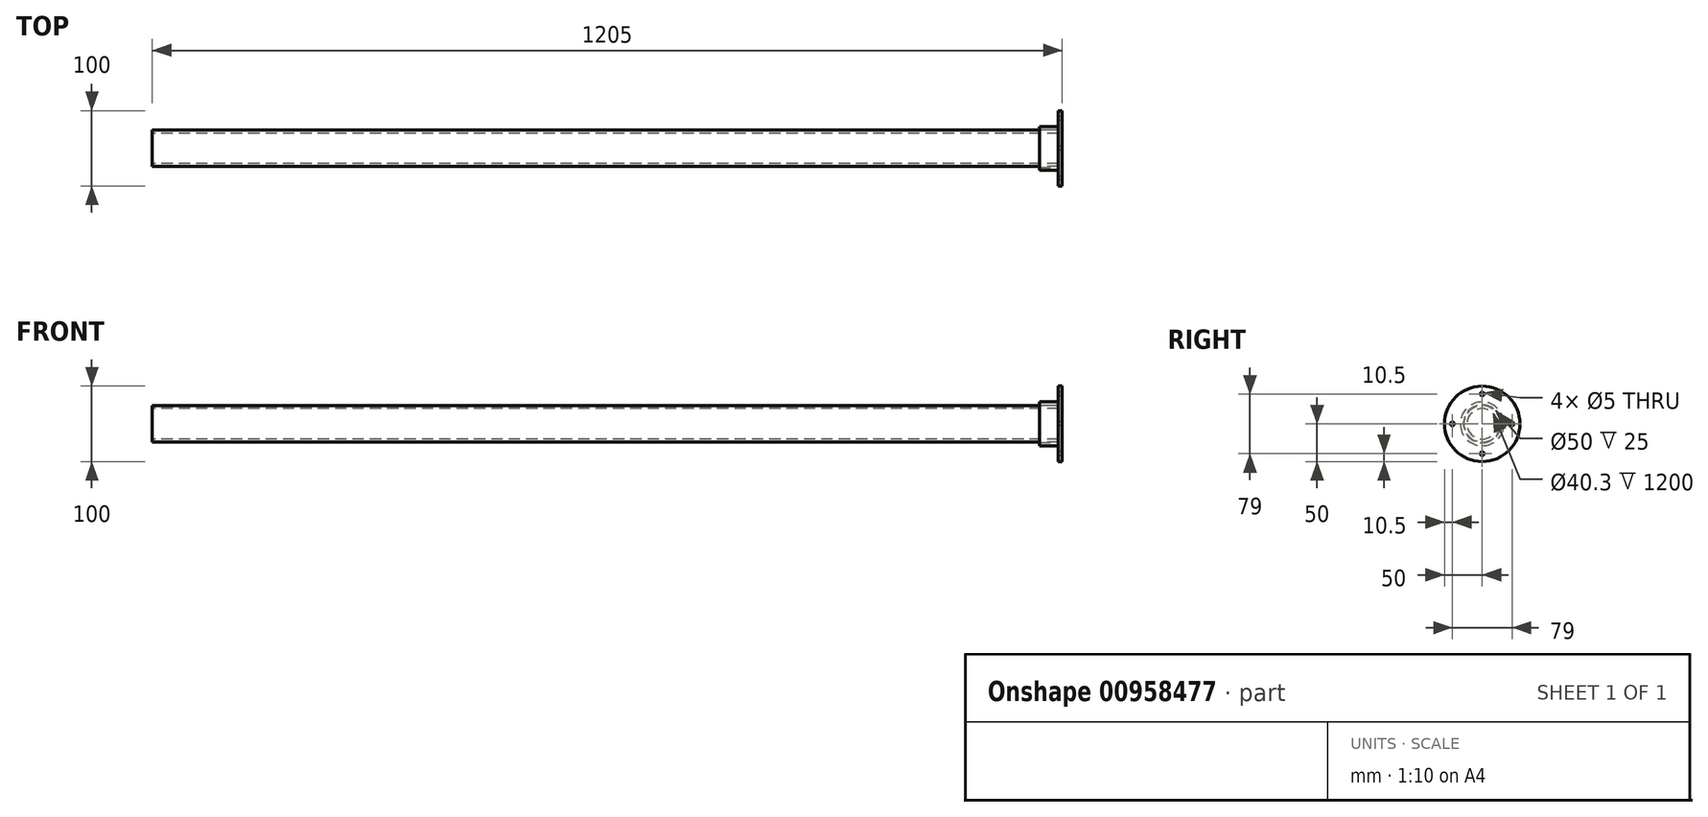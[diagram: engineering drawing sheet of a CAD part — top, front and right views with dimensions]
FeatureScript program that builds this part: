
annotation { "Feature Type Name" : "Feature", "Feature Type Description" : "" }
export const myFeature = defineFeature(function(context is Context, id is Id, definition is map)
    precondition{}
    {
        {
            var Q0;
            Q0=qCreatedBy(makeId("Right.planeOp"),FACE);
            var sketch = newSketch(context, id + "F0", { "sketchPlane" : qUnion([Q0])});
            skCircle(sketch, "E0", {"center": v(0, 0) * mm, "radius": 24.15 * mm});
            skCircle(sketch, "E1", {"center": v(0, 0) * mm, "radius": 20.15 * mm});
            skSolve(sketch);
        }
        {
            var Q0;
            Q0 = qSketchRegion(id + "F0", true);
            extrude(context, id + "F1", {"entities" : qUnion([Q0]), "depth" : 1200 * mm, "offsetDistance" : 25 * mm});
        }
        {
            var Q0;
            Q0=makeQuery(id+"F1.opExtrude","CAP_FACE",FACE,{"disambiguationData":[OSD([sQuery(id+"F0.wireOp",EDGE,"E0"),sQuery(id+"F0.wireOp",EDGE,"E1")])],"isStart":false});
            var sketch = newSketch(context, id + "F2", { "sketchPlane" : qUnion([Q0])});
            skCircle(sketch, "E2", {"center": v(0, 0) * mm, "radius": 50 * mm});
            skSolve(sketch);
        }
        {
            var Q0;
            Q0 = qSketchRegion(id + "F2", true);
            extrude(context, id + "F3", {"entities" : qUnion([Q0]), "depth" : 5 * mm, "offsetDistance" : 25 * mm});
        }
        {
            var Q0;
            Q0=makeQuery(id+"F3.opExtrude","CAP_FACE",FACE,{"disambiguationData":[OSD([sQuery(id+"F2.wireOp",EDGE,"E2")])],"isStart":true});
            var sketch = newSketch(context, id + "F4", { "sketchPlane" : qUnion([Q0])});
            skCircle(sketch, "E3", {"center": v(0, 0) * mm, "radius": 25 * mm});
            skCircle(sketch, "E4", {"center": v(0, 0) * mm, "radius": 29 * mm});
            skSolve(sketch);
        }
        {
            var Q0;
            Q0 = qSketchRegion(id + "F4", true);
            extrude(context, id + "F5", {"entities" : qUnion([Q0]), "operationType" : NewBodyOperationType.ADD, "depth" : 25 * mm, "offsetDistance" : 25 * mm});
        }
        {
            var Q0;
            {var subQ0=sQuery(id+"F2.wireOp",EDGE,"E2");Q0=makeQuery(id+"F5.boolean.opBoolean","SPLIT",FACE,{"disambiguationData":[TD([makeQuery(id+"F3.opExtrude","SWEPT_FACE",FACE,{"disambiguationData":[OSD([subQ0])]})])],"derivedFrom":makeQuery(id+"F3.opExtrude","CAP_FACE",FACE,{"disambiguationData":[OSD([subQ0])],"isStart":true})});}
            var sketch = newSketch(context, id + "F6", { "sketchPlane" : qUnion([Q0])});
            skCircle(sketch, "E5", {"center": v(0, 0) * mm, "radius": 39.5 * mm, "construction": true});
            skCircle(sketch, "E6", {"center": v(-39.5, 0) * mm, "radius": 2.5 * mm});
            skCircle(sketch, "E7", {"center": v(39.5, 0) * mm, "radius": 2.5 * mm});
            skCircle(sketch, "E8", {"center": v(0, 39.5) * mm, "radius": 2.5 * mm});
            skCircle(sketch, "E9", {"center": v(0, -39.5) * mm, "radius": 2.5 * mm});
            skSolve(sketch);
        }
        {
            var Q0;
            Q0 = qSketchRegion(id + "F6", true);
            extrude(context, id + "F7", {"entities" : qUnion([Q0]), "operationType" : NewBodyOperationType.REMOVE, "endBound" : BoundingType.UP_TO_NEXT, "oppositeDirection" : true, "depth" : 25 * mm, "offsetDistance" : 25 * mm});
        }
    });
